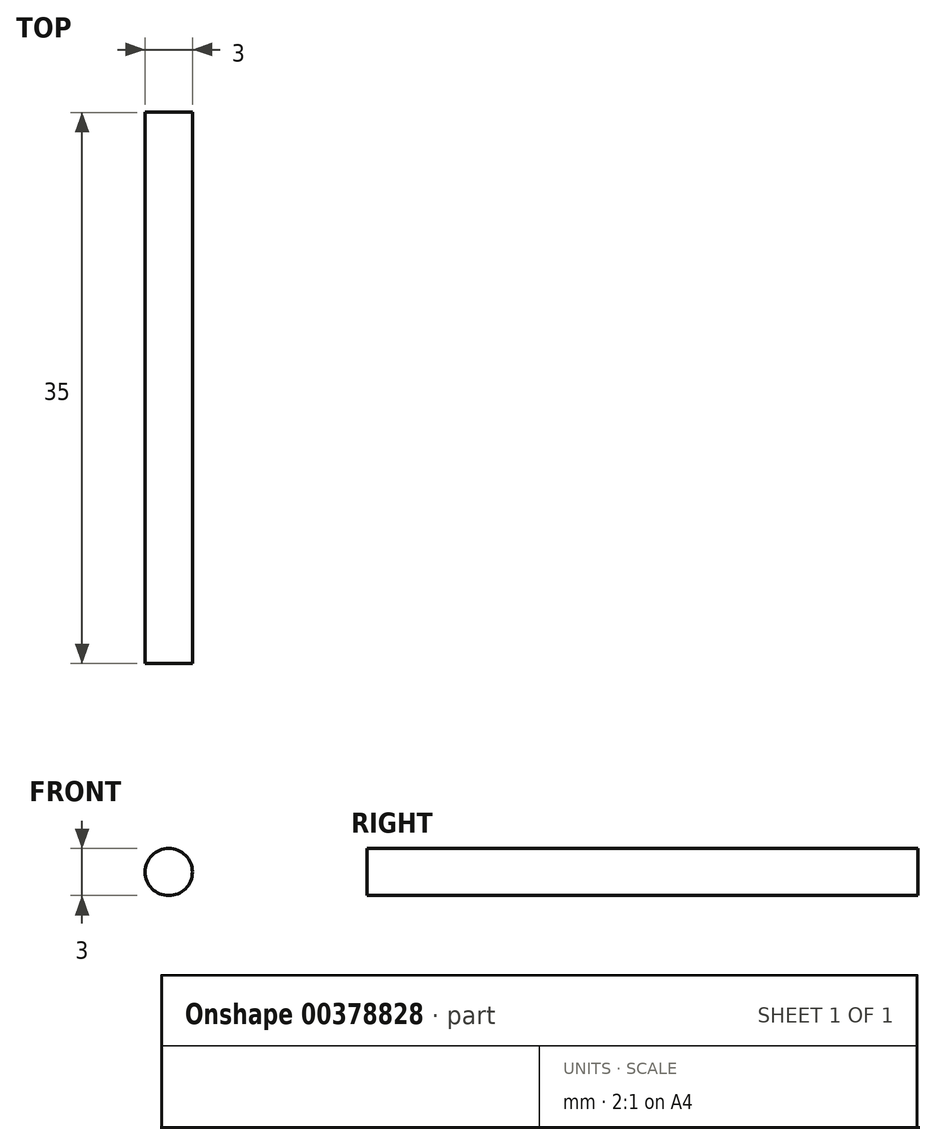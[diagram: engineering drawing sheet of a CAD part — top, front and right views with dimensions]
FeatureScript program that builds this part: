
annotation { "Feature Type Name" : "Feature", "Feature Type Description" : "" }
export const myFeature = defineFeature(function(context is Context, id is Id, definition is map)
    precondition{}
    {
        {
            var Q0;
            Q0=qCreatedBy(makeId("Top.planeOp"),FACE);
            var sketch = newSketch(context, id + "F0", { "sketchPlane" : qUnion([Q0])});
            skLineSegment(sketch, "E0.bottom", {"start": v(-19.14, 56.11) * mm, "end": v(-17.64, 56.11) * mm});
            skLineSegment(sketch, "E0.top", {"start": v(-19.14, 21.11) * mm, "end": v(-17.64, 21.11) * mm});
            skLineSegment(sketch, "E0.left", {"start": v(-19.14, 56.11) * mm, "end": v(-19.14, 21.11) * mm});
            skLineSegment(sketch, "E0.right", {"start": v(-17.64, 56.11) * mm, "end": v(-17.64, 21.11) * mm});
            skSolve(sketch);
        }
        {
            var Q0;
            Q0=makeQuery(id+"F0.imprint","IMPRINT",FACE,{"disambiguationData":[TD([[makeQuery(id+"F0.imprint","IMPRINT",EDGE,{"derivedFrom":sQuery(id+"F0.wireOp",EDGE,"E0.bottom")}),-1.0]])]});
            var Q1;
            Q1=sQuery(id+"F0.wireOp",EDGE,"E0.right");
            revolve(context, id + "F1", {"entities" : qUnion([Q0]), "axis" : qUnion([Q1]), "revolveType" : RevolveType.FULL});
        }
    });
